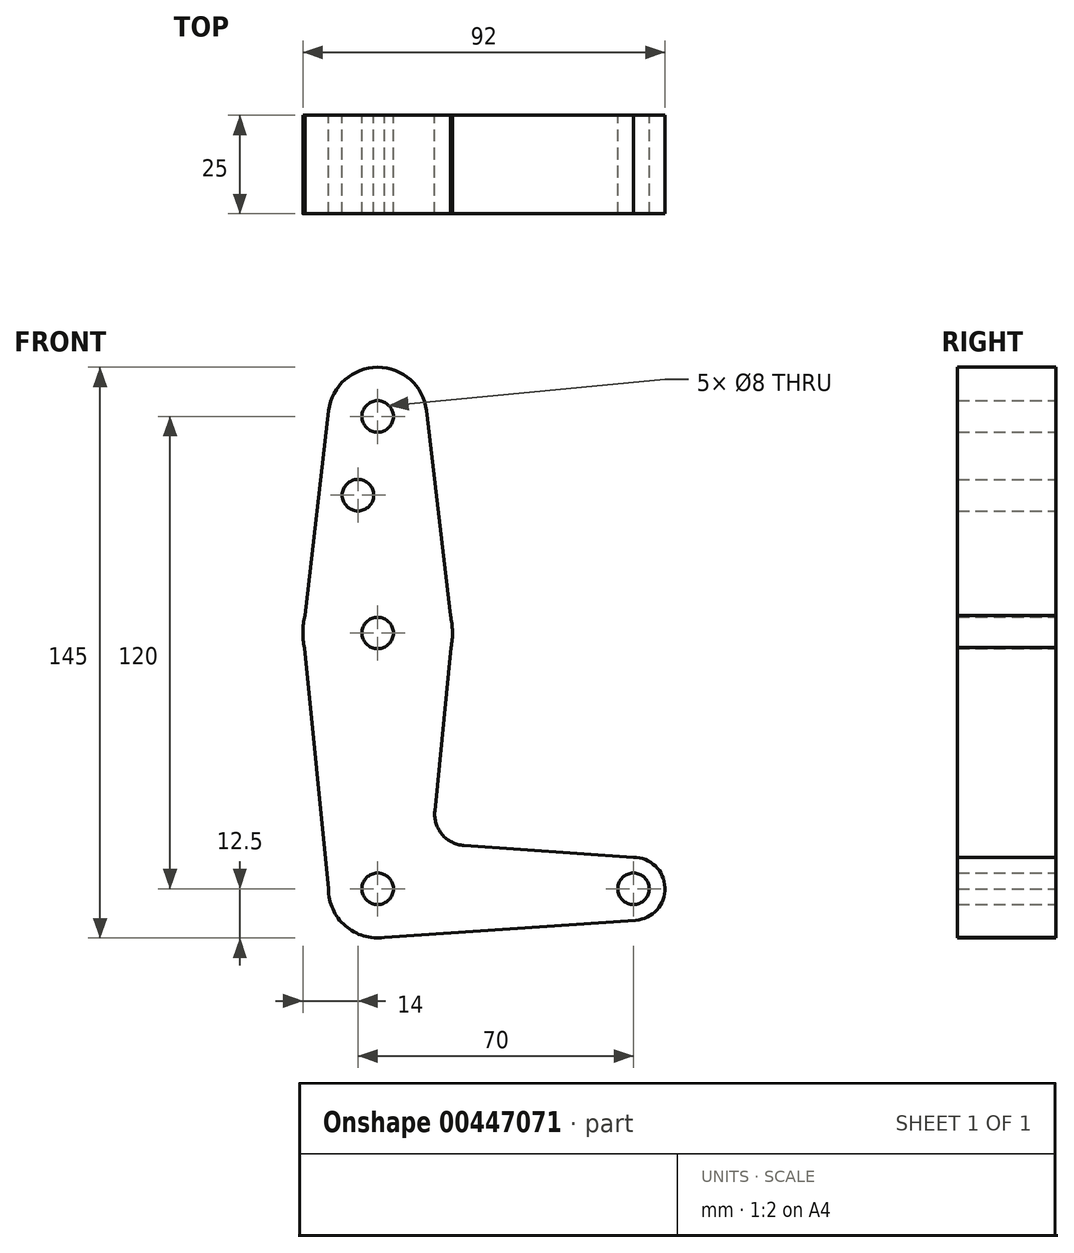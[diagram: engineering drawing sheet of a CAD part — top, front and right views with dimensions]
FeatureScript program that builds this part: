
annotation { "Feature Type Name" : "Feature", "Feature Type Description" : "" }
export const myFeature = defineFeature(function(context is Context, id is Id, definition is map)
    precondition{}
    {
        {
            var Q0;
            Q0=qCreatedBy(makeId("Front.planeOp"),FACE);
            var sketch = newSketch(context, id + "F0", { "sketchPlane" : qUnion([Q0])});
            skLineSegment(sketch, "E0", {"start": v(0, 0) * mm, "end": v(0, 120) * mm, "construction": true});
            skLineSegment(sketch, "E1", {"start": v(0, 0) * mm, "end": v(65, 0) * mm, "construction": true});
            skCircle(sketch, "E2", {"center": v(0, 0) * mm, "radius": 12.5 * mm});
            skCircle(sketch, "E3", {"center": v(65, 0) * mm, "radius": 8 * mm});
            skCircle(sketch, "E4", {"center": v(0, 120) * mm, "radius": 12.5 * mm});
            skCircle(sketch, "E5", {"center": v(0, 65) * mm, "radius": 19 * mm});
            skLineSegment(sketch, "E6", {"start": v(0, -12.5) * mm, "end": v(65.55, -7.98) * mm});
            skCircle(sketch, "E7", {"center": v(0, 120) * mm, "radius": 4 * mm});
            skCircle(sketch, "E8", {"center": v(-5, 100) * mm, "radius": 4 * mm});
            skCircle(sketch, "E9", {"center": v(0, 65) * mm, "radius": 4 * mm});
            skCircle(sketch, "E10", {"center": v(0, 0) * mm, "radius": 4 * mm});
            skCircle(sketch, "E11", {"center": v(65, 0) * mm, "radius": 4 * mm});
            skLineSegment(sketch, "E12", {"start": v(19, 65) * mm, "end": v(12.42, 121.45) * mm});
            skLineSegment(sketch, "E13", {"start": v(-12.42, 121.45) * mm, "end": v(-19, 65) * mm});
            skLineSegment(sketch, "E14", {"start": v(19, 65) * mm, "end": v(14.52, 19.77) * mm});
            skLineSegment(sketch, "E15", {"start": v(-12.5, 0) * mm, "end": v(-19, 65) * mm});
            skLineSegment(sketch, "E16", {"start": v(65, 8) * mm, "end": v(21.92, 11) * mm});
            skPoint(sketch, "E17.newPointA", {"position": v(0, 12.53) * mm});
            skArc(sketch, "E17.filletArc", {"start": v(14.52, 19.77) * mm, "mid": v(16.37, 13.82) * mm, "end": v(21.92, 11) * mm});
            skSolve(sketch);
        }
        {
            var Q0;
            Q0 = qSketchRegion(id + "F0", true);
            extrude(context, id + "F1", {"entities" : qUnion([Q0]), "depth" : 25 * mm});
        }
    });
